# Revit family: CENTUM Profil XL 120 6m quer L2D
name_source: partatom
category: HLS-Bauteile
units: mm (PartAtom-declared; Revit-internal decimal feet)

## family parameters
Arbeitsebenenbasiert = Ja
Beim Laden mit Abzugskörper schneiden = Nein
Bemaßung runder Anschluss = Durchmesser verwenden
Beschriftungsausrichtung beibehalten = Nein
Gemeinsam genutzt = Ja
Immer vertikal = Nein
Raumberechnungspunkt = Nein
Teiletyp = Normal

## types (1)
- Centum Profil XL120 L=6000 L2D
    Abmessung = 100/120/4.0 mm
    Artikelnummer = 16012060
    Breite = 100 mm  [stored 0.328084 ft]
    Bund = 72 m
    EAN = 4250928436641
    Fabrikat = MEFA
    Firma = MEFA Befestigungs- und Montagesysteme GmbH
    Fläche (schwächster Profilquerschnitt) = 0 m²
    Gewicht = 12,20 kg
    Höhe = 120 mm
    Kurztext1 = Montageprofil CENTUM XL 120
    Kurztext2 = 100 / 120 / 4 mm L= 6 m fsv
    Langloch = 14.0 x 65.0 mm
    Länge = 6000 mm  [stored 19.685 ft]
    Material = Stahl
    Materialname = S275
    Mengeneinheit = m
    Oberflaeche = feuerstückverzinkt
    Profil = CENTUM
    Profiltyp = XL 120
    Streckgrenze = 235 N/mm²
    Stärke = 4 mm  [stored 0.0131234 ft]
    Torsionswiderstandsmoment Wt = 89.10 cm³
    Trägheitsradius iy = 4.64 cm
    Trägheitsradius iz = 4.05 cm
    Vorgabe-Ansicht = 1219 mm
    Widerstandsmoment Wy = 51.76 cm³
    Widerstandsmoment Wz = 47.44 cm³
    vpe = 6

note: [stored X ft] marks values corroborated as IEEE doubles in the binary element streams (Revit-internal decimal feet)
